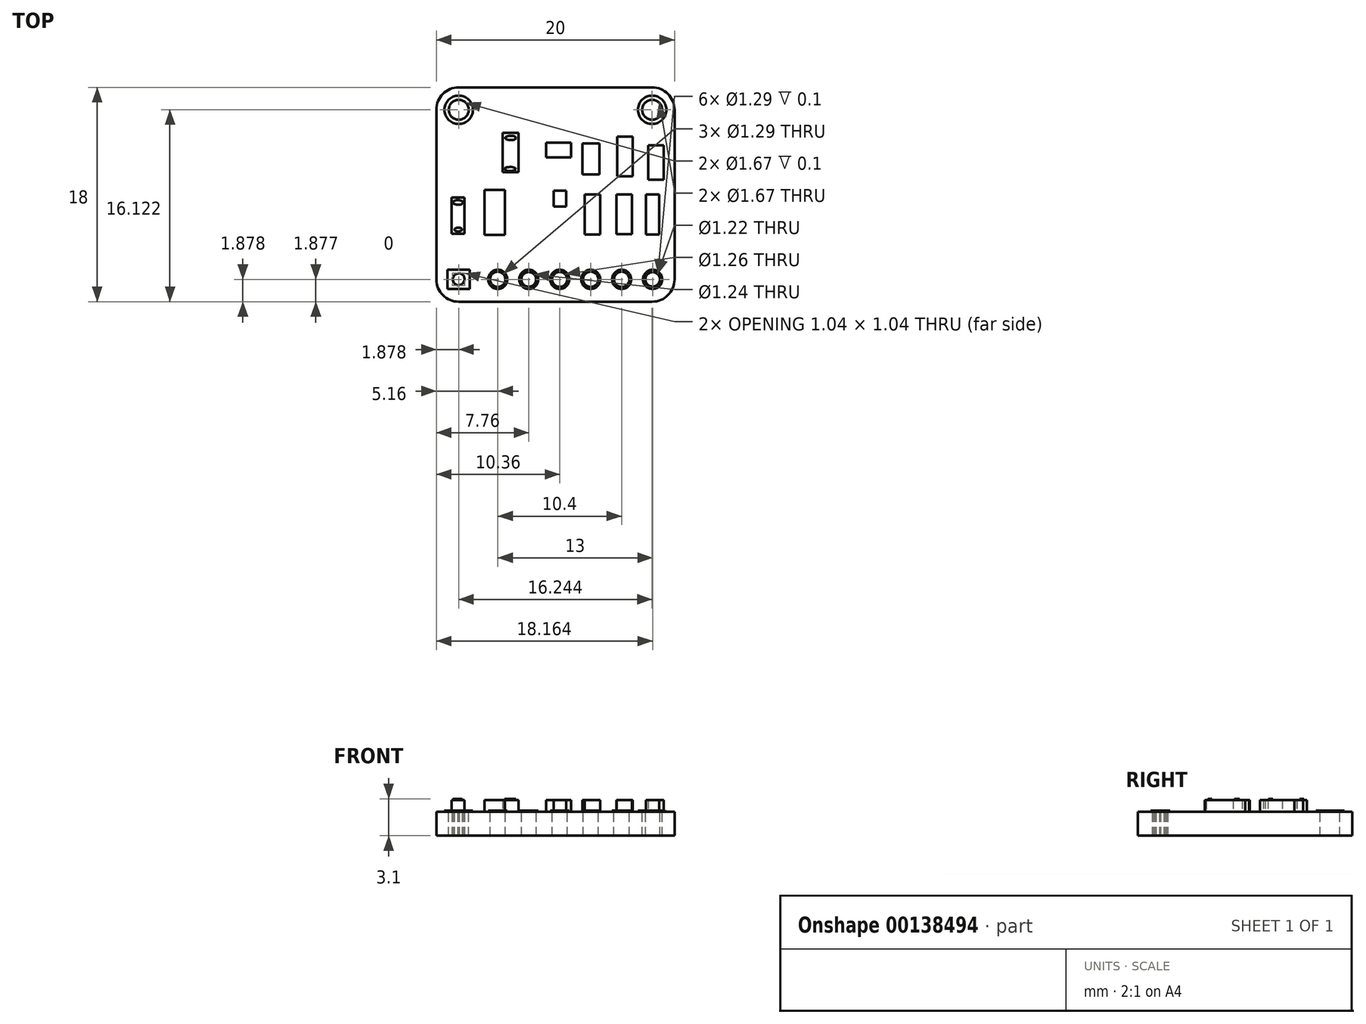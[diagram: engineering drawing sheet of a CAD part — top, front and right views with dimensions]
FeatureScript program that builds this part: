
annotation { "Feature Type Name" : "Feature", "Feature Type Description" : "" }
export const myFeature = defineFeature(function(context is Context, id is Id, definition is map)
    precondition{}
    {
        {
            var Q0;
            Q0=qCreatedBy(makeId("Top.planeOp"),FACE);
            var sketch = newSketch(context, id + "F0", { "sketchPlane" : qUnion([Q0])});
            skLineSegment(sketch, "E0.bottom", {"start": v(10, 9) * mm, "end": v(-10, 9) * mm});
            skLineSegment(sketch, "E0.top", {"start": v(10, -9) * mm, "end": v(-10, -9) * mm});
            skLineSegment(sketch, "E0.left", {"start": v(10, 9) * mm, "end": v(10, -9) * mm});
            skLineSegment(sketch, "E0.right", {"start": v(-10, 9) * mm, "end": v(-10, -9) * mm});
            skPoint(sketch, "E0.middle", {"position": v(0, 0) * mm});
            skSolve(sketch);
        }
        {
            var Q0;
            Q0 = qSketchRegion(id + "F0", true);
            extrude(context, id + "F1", {"entities" : qUnion([Q0]), "oppositeDirection" : true, "depth" : 2 * mm});
        }
        {
            var Q0;
            Q0=makeQuery(id+"F1.opExtrude","SWEPT_EDGE",EDGE,{"disambiguationData":[OSD([sQuery(id+"F0.wireOp",EDGE,"E0.top"),sQuery(id+"F0.wireOp",EDGE,"E0.right")])]});
            var Q1;
            Q1=makeQuery(id+"F1.opExtrude","SWEPT_EDGE",EDGE,{"disambiguationData":[OSD([sQuery(id+"F0.wireOp",EDGE,"E0.top"),sQuery(id+"F0.wireOp",EDGE,"E0.left")])]});
            var Q2;
            Q2=makeQuery(id+"F1.opExtrude","SWEPT_EDGE",EDGE,{"disambiguationData":[OSD([sQuery(id+"F0.wireOp",EDGE,"E0.bottom"),sQuery(id+"F0.wireOp",EDGE,"E0.left")])]});
            var Q3;
            Q3=makeQuery(id+"F1.opExtrude","SWEPT_EDGE",EDGE,{"disambiguationData":[OSD([sQuery(id+"F0.wireOp",EDGE,"E0.bottom"),sQuery(id+"F0.wireOp",EDGE,"E0.right")])]});
            fillet(context, id + "F2", {"entities" : qUnion([Q0, Q1, Q2, Q3]), "radius" : 1.88 * mm, "tangentPropagation" : true, "allowEdgeOverflow" : false});
        }
        {
            var Q0;
            Q0=makeQuery(id+"F1.opExtrude","CAP_FACE",FACE,{"disambiguationData":[OSD([sQuery(id+"F0.wireOp",EDGE,"E0.bottom"),sQuery(id+"F0.wireOp",EDGE,"E0.top"),sQuery(id+"F0.wireOp",EDGE,"E0.left"),sQuery(id+"F0.wireOp",EDGE,"E0.right")])],"isStart":true});
            var sketch = newSketch(context, id + "F3", { "sketchPlane" : qUnion([Q0])});
            skLineSegment(sketch, "E1", {"start": v(-10, 7.12) * mm, "end": v(10, 7.12) * mm, "construction": true});
            skCircle(sketch, "E2", {"center": v(-8.12, 7.12) * mm, "radius": 1.2 * mm});
            skCircle(sketch, "E3", {"center": v(8.12, 7.12) * mm, "radius": 1.2 * mm});
            skCircle(sketch, "E4", {"center": v(-8.12, 7.12) * mm, "radius": 0.84 * mm});
            skCircle(sketch, "E5", {"center": v(8.12, 7.12) * mm, "radius": 0.84 * mm});
            skLineSegment(sketch, "E6", {"start": v(-10, -7.12) * mm, "end": v(10, -7.12) * mm, "construction": true});
            skLineSegment(sketch, "E7.bottom", {"start": v(-7.18, -6.3) * mm, "end": v(-9.06, -6.3) * mm});
            skLineSegment(sketch, "E7.top", {"start": v(-7.18, -7.94) * mm, "end": v(-9.06, -7.94) * mm});
            skLineSegment(sketch, "E7.left", {"start": v(-7.18, -6.3) * mm, "end": v(-7.18, -7.94) * mm});
            skLineSegment(sketch, "E7.right", {"start": v(-9.06, -6.3) * mm, "end": v(-9.06, -7.94) * mm});
            skPoint(sketch, "E7.middle", {"position": v(-8.12, -7.12) * mm});
            skCircle(sketch, "E8.cCircle", {"center": v(-8.12, -7.12) * mm, "radius": 0.48 * mm, "construction": true});
            skLineSegment(sketch, "E8.0", {"start": v(-8.07, -6.6) * mm, "end": v(-7.71, -6.8) * mm});
            skLineSegment(sketch, "E8.1", {"start": v(-7.71, -6.8) * mm, "end": v(-7.6, -7.18) * mm});
            skLineSegment(sketch, "E8.2", {"start": v(-7.6, -7.18) * mm, "end": v(-7.8, -7.53) * mm});
            skLineSegment(sketch, "E8.3", {"start": v(-7.8, -7.53) * mm, "end": v(-8.18, -7.64) * mm});
            skLineSegment(sketch, "E8.4", {"start": v(-8.18, -7.64) * mm, "end": v(-8.53, -7.45) * mm});
            skLineSegment(sketch, "E8.5", {"start": v(-8.53, -7.45) * mm, "end": v(-8.64, -7.07) * mm});
            skLineSegment(sketch, "E8.6", {"start": v(-8.64, -7.07) * mm, "end": v(-8.45, -6.71) * mm});
            skLineSegment(sketch, "E8.7", {"start": v(-8.45, -6.71) * mm, "end": v(-8.07, -6.6) * mm});
            skPoint(sketch, "E8.0.midPoint", {"position": v(-7.9, -6.7) * mm});
            skCircle(sketch, "E9", {"center": v(-4.84, -7.12) * mm, "radius": 0.8 * mm});
            skCircle(sketch, "E10", {"center": v(-2.24, -7.12) * mm, "radius": 0.8 * mm});
            skCircle(sketch, "E11", {"center": v(0.36, -7.12) * mm, "radius": 0.8 * mm});
            skCircle(sketch, "E12", {"center": v(2.96, -7.12) * mm, "radius": 0.8 * mm});
            skCircle(sketch, "E13", {"center": v(5.56, -7.12) * mm, "radius": 0.8 * mm});
            skCircle(sketch, "E14", {"center": v(8.16, -7.12) * mm, "radius": 0.8 * mm});
            skCircle(sketch, "E15", {"center": v(-4.84, -7.12) * mm, "radius": 0.64 * mm});
            skCircle(sketch, "E16", {"center": v(-2.24, -7.12) * mm, "radius": 0.64 * mm});
            skCircle(sketch, "E17", {"center": v(0.36, -7.12) * mm, "radius": 0.64 * mm});
            skCircle(sketch, "E18", {"center": v(2.96, -7.12) * mm, "radius": 0.64 * mm});
            skCircle(sketch, "E19", {"center": v(5.56, -7.12) * mm, "radius": 0.64 * mm});
            skCircle(sketch, "E20", {"center": v(8.16, -7.12) * mm, "radius": 0.64 * mm});
            skCircle(sketch, "E21", {"center": v(-4.84, -7.12) * mm, "radius": 0.6 * mm});
            skCircle(sketch, "E22", {"center": v(-2.24, -7.12) * mm, "radius": 0.62 * mm});
            skCircle(sketch, "E23", {"center": v(0.36, -7.12) * mm, "radius": 0.63 * mm});
            skCircle(sketch, "E24", {"center": v(2.96, -7.12) * mm, "radius": 0.59 * mm});
            skCircle(sketch, "E25", {"center": v(5.56, -7.12) * mm, "radius": 0.6 * mm});
            skCircle(sketch, "E26", {"center": v(8.16, -7.12) * mm, "radius": 0.61 * mm});
            skSolve(sketch);
        }
        {
            var Q0;
            Q0=makeQuery(id+"F3.imprint","IMPRINT",FACE,{"disambiguationData":[TD([[makeQuery(id+"F3.imprint","IMPRINT",EDGE,{"derivedFrom":sQuery(id+"F3.wireOp",EDGE,"E9")}),1.0]])]});
            var Q1;
            Q1=makeQuery(id+"F3.imprint","IMPRINT",FACE,{"disambiguationData":[TD([[makeQuery(id+"F3.imprint","IMPRINT",EDGE,{"derivedFrom":sQuery(id+"F3.wireOp",EDGE,"E10")}),1.0]])]});
            var Q2;
            Q2=makeQuery(id+"F3.imprint","IMPRINT",FACE,{"disambiguationData":[TD([[makeQuery(id+"F3.imprint","IMPRINT",EDGE,{"derivedFrom":sQuery(id+"F3.wireOp",EDGE,"E11")}),1.0]])]});
            var Q3;
            Q3=makeQuery(id+"F3.imprint","IMPRINT",FACE,{"disambiguationData":[TD([[makeQuery(id+"F3.imprint","IMPRINT",EDGE,{"derivedFrom":sQuery(id+"F3.wireOp",EDGE,"E12")}),1.0]])]});
            var Q4;
            Q4=makeQuery(id+"F3.imprint","IMPRINT",FACE,{"disambiguationData":[TD([[makeQuery(id+"F3.imprint","IMPRINT",EDGE,{"derivedFrom":sQuery(id+"F3.wireOp",EDGE,"E13")}),1.0]])]});
            var Q5;
            Q5=makeQuery(id+"F3.imprint","IMPRINT",FACE,{"disambiguationData":[TD([[makeQuery(id+"F3.imprint","IMPRINT",EDGE,{"derivedFrom":sQuery(id+"F3.wireOp",EDGE,"E14")}),1.0]])]});
            var Q6;
            Q6=makeQuery(id+"F3.imprint","IMPRINT",FACE,{"disambiguationData":[TD([[makeQuery(id+"F3.imprint","IMPRINT",EDGE,{"derivedFrom":sQuery(id+"F3.wireOp",EDGE,"E7.bottom")}),1.0]])]});
            var Q7;
            Q7=makeQuery(id+"F3.imprint","IMPRINT",FACE,{"disambiguationData":[TD([[makeQuery(id+"F3.imprint","IMPRINT",EDGE,{"derivedFrom":sQuery(id+"F3.wireOp",EDGE,"E3")}),1.0]])]});
            var Q8;
            Q8=makeQuery(id+"F3.imprint","IMPRINT",FACE,{"disambiguationData":[TD([[makeQuery(id+"F3.imprint","IMPRINT",EDGE,{"derivedFrom":sQuery(id+"F3.wireOp",EDGE,"E2")}),1.0]])]});
            extrude(context, id + "F4", {"entities" : qUnion([Q0, Q1, Q2, Q3, Q4, Q5, Q6, Q7, Q8]), "depth" : .1 * mm});
        }
        {
            var Q0;
            Q0=makeQuery(id+"F3.imprint","IMPRINT",FACE,{"disambiguationData":[TD([[makeQuery(id+"F3.imprint","IMPRINT",EDGE,{"derivedFrom":sQuery(id+"F3.wireOp",EDGE,"E15")}),1.0]])]});
            var Q1;
            Q1=makeQuery(id+"F3.imprint","IMPRINT",FACE,{"disambiguationData":[TD([[makeQuery(id+"F3.imprint","IMPRINT",EDGE,{"derivedFrom":sQuery(id+"F3.wireOp",EDGE,"E8.0")}),-1.0]])]});
            var Q2;
            Q2=makeQuery(id+"F3.imprint","IMPRINT",FACE,{"disambiguationData":[TD([[makeQuery(id+"F3.imprint","IMPRINT",EDGE,{"derivedFrom":sQuery(id+"F3.wireOp",EDGE,"E22")}),1.0]])]});
            var Q3;
            Q3=makeQuery(id+"F3.imprint","IMPRINT",FACE,{"disambiguationData":[TD([[makeQuery(id+"F3.imprint","IMPRINT",EDGE,{"derivedFrom":sQuery(id+"F3.wireOp",EDGE,"E18")}),1.0]])]});
            var Q4;
            Q4=makeQuery(id+"F3.imprint","IMPRINT",FACE,{"disambiguationData":[TD([[makeQuery(id+"F3.imprint","IMPRINT",EDGE,{"derivedFrom":sQuery(id+"F3.wireOp",EDGE,"E23")}),1.0]])]});
            var Q5;
            Q5=makeQuery(id+"F3.imprint","IMPRINT",FACE,{"disambiguationData":[TD([[makeQuery(id+"F3.imprint","IMPRINT",EDGE,{"derivedFrom":sQuery(id+"F3.wireOp",EDGE,"E19")}),1.0]])]});
            var Q6;
            Q6=makeQuery(id+"F3.imprint","IMPRINT",FACE,{"disambiguationData":[TD([[makeQuery(id+"F3.imprint","IMPRINT",EDGE,{"derivedFrom":sQuery(id+"F3.wireOp",EDGE,"E26")}),1.0]])]});
            var Q7;
            Q7=makeQuery(id+"F3.imprint","IMPRINT",FACE,{"disambiguationData":[TD([[makeQuery(id+"F3.imprint","IMPRINT",EDGE,{"derivedFrom":sQuery(id+"F3.wireOp",EDGE,"E21")}),1.0]])]});
            var Q8;
            Q8=makeQuery(id+"F3.imprint","IMPRINT",FACE,{"disambiguationData":[TD([[makeQuery(id+"F3.imprint","IMPRINT",EDGE,{"derivedFrom":sQuery(id+"F3.wireOp",EDGE,"E24")}),1.0]])]});
            var Q9;
            Q9=makeQuery(id+"F3.imprint","IMPRINT",FACE,{"disambiguationData":[TD([[makeQuery(id+"F3.imprint","IMPRINT",EDGE,{"derivedFrom":sQuery(id+"F3.wireOp",EDGE,"E25")}),1.0]])]});
            var Q10;
            Q10=makeQuery(id+"F3.imprint","IMPRINT",FACE,{"disambiguationData":[TD([[makeQuery(id+"F3.imprint","IMPRINT",EDGE,{"derivedFrom":sQuery(id+"F3.wireOp",EDGE,"E5")}),1.0]])]});
            var Q11;
            Q11=makeQuery(id+"F3.imprint","IMPRINT",FACE,{"disambiguationData":[TD([[makeQuery(id+"F3.imprint","IMPRINT",EDGE,{"derivedFrom":sQuery(id+"F3.wireOp",EDGE,"E4")}),1.0]])]});
            extrude(context, id + "F5", {"entities" : qUnion([Q0, Q1, Q2, Q3, Q4, Q5, Q6, Q7, Q8, Q9, Q10, Q11]), "operationType" : NewBodyOperationType.REMOVE, "oppositeDirection" : true, "depth" : 25 * mm});
        }
        {
            var Q0;
            Q0=makeQuery(id+"F3.imprint","IMPRINT",FACE,{"disambiguationData":[TD([[makeQuery(id+"F3.imprint","IMPRINT",EDGE,{"derivedFrom":sQuery(id+"F3.wireOp",EDGE,"E2")}),-1.0]])]});
            var sketch = newSketch(context, id + "F6", { "sketchPlane" : qUnion([Q0])});
            skLineSegment(sketch, "E27", {"start": v(-4.87, -7.14) * mm, "end": v(-4.87, 7.87) * mm, "construction": true});
            skLineSegment(sketch, "E28", {"start": v(-2.22, -7.15) * mm, "end": v(-2.22, 8) * mm, "construction": true});
            skLineSegment(sketch, "E29", {"start": v(0.38, -7.12) * mm, "end": v(0.38, 7.8) * mm, "construction": true});
            skLineSegment(sketch, "E30", {"start": v(2.9, -7.2) * mm, "end": v(2.9, 7.83) * mm, "construction": true});
            skLineSegment(sketch, "E31", {"start": v(5.53, -7.1) * mm, "end": v(5.53, 7.94) * mm, "construction": true});
            skLineSegment(sketch, "E32", {"start": v(8.22, -7.12) * mm, "end": v(8.22, 7.43) * mm, "construction": true});
            skLineSegment(sketch, "E33", {"start": v(-9.22, -2.26) * mm, "end": v(9.5, -2.26) * mm, "construction": true});
            skLineSegment(sketch, "E34", {"start": v(-6.74, 3.73) * mm, "end": v(9.34, 3.73) * mm, "construction": true});
            skLineSegment(sketch, "E35.bottom", {"start": v(-8.71, -3.28) * mm, "end": v(-7.63, -3.28) * mm});
            skLineSegment(sketch, "E35.top", {"start": v(-8.71, -0.25) * mm, "end": v(-7.63, -0.25) * mm});
            skLineSegment(sketch, "E35.left", {"start": v(-8.71, -3.28) * mm, "end": v(-8.71, -0.25) * mm});
            skLineSegment(sketch, "E35.right", {"start": v(-7.63, -3.28) * mm, "end": v(-7.63, -0.25) * mm});
            skLineSegment(sketch, "E36.bottom", {"start": v(-5.97, -3.4) * mm, "end": v(-4.24, -3.4) * mm});
            skLineSegment(sketch, "E36.top", {"start": v(-5.97, 0.38) * mm, "end": v(-4.24, 0.38) * mm});
            skLineSegment(sketch, "E36.left", {"start": v(-5.97, -3.4) * mm, "end": v(-5.97, 0.38) * mm});
            skLineSegment(sketch, "E36.right", {"start": v(-4.24, -3.4) * mm, "end": v(-4.24, 0.38) * mm});
            skLineSegment(sketch, "E37.bottom", {"start": v(-4.42, 1.9) * mm, "end": v(-3.09, 1.9) * mm});
            skLineSegment(sketch, "E37.top", {"start": v(-4.42, 5.18) * mm, "end": v(-3.09, 5.18) * mm});
            skLineSegment(sketch, "E37.left", {"start": v(-4.42, 1.9) * mm, "end": v(-4.42, 5.18) * mm});
            skLineSegment(sketch, "E37.right", {"start": v(-3.09, 1.9) * mm, "end": v(-3.09, 5.18) * mm});
            skLineSegment(sketch, "E38.bottom", {"start": v(0.9, 0.31) * mm, "end": v(-0.14, 0.31) * mm});
            skLineSegment(sketch, "E38.top", {"start": v(0.9, -1.02) * mm, "end": v(-0.14, -1.02) * mm});
            skLineSegment(sketch, "E38.left", {"start": v(0.9, 0.31) * mm, "end": v(0.9, -1.02) * mm});
            skPoint(sketch, "E39.firstSnap0", {"position": v(1.3, 3.73) * mm});
            skLineSegment(sketch, "E39.bottom", {"start": v(1.3, 4.35) * mm, "end": v(-0.78, 4.35) * mm});
            skLineSegment(sketch, "E39.top", {"start": v(1.3, 3.12) * mm, "end": v(-0.78, 3.12) * mm});
            skLineSegment(sketch, "E39.left", {"start": v(1.3, 4.35) * mm, "end": v(1.3, 3.12) * mm});
            skLineSegment(sketch, "E39.right", {"start": v(-0.78, 4.35) * mm, "end": v(-0.78, 3.12) * mm});
            skLineSegment(sketch, "E40.bottom", {"start": v(3.7, 4.31) * mm, "end": v(2.28, 4.31) * mm});
            skLineSegment(sketch, "E40.top", {"start": v(3.7, 1.68) * mm, "end": v(2.28, 1.68) * mm});
            skLineSegment(sketch, "E40.left", {"start": v(3.7, 4.31) * mm, "end": v(3.7, 1.68) * mm});
            skLineSegment(sketch, "E40.right", {"start": v(2.28, 4.31) * mm, "end": v(2.28, 1.68) * mm});
            skLineSegment(sketch, "E41.bottom", {"start": v(2.46, -3.34) * mm, "end": v(3.77, -3.34) * mm});
            skLineSegment(sketch, "E41.top", {"start": v(2.46, 0) * mm, "end": v(3.77, 0) * mm});
            skLineSegment(sketch, "E41.left", {"start": v(2.46, -3.34) * mm, "end": v(2.46, 0) * mm});
            skLineSegment(sketch, "E41.right", {"start": v(3.77, -3.34) * mm, "end": v(3.77, 0) * mm});
            skLineSegment(sketch, "E42.bottom", {"start": v(5.12, 0) * mm, "end": v(6.42, 0) * mm});
            skLineSegment(sketch, "E42.top", {"start": v(5.12, -3.33) * mm, "end": v(6.42, -3.33) * mm});
            skLineSegment(sketch, "E42.left", {"start": v(5.12, 0) * mm, "end": v(5.12, -3.33) * mm});
            skLineSegment(sketch, "E42.right", {"start": v(6.42, 0) * mm, "end": v(6.42, -3.33) * mm});
            skLineSegment(sketch, "E43.bottom", {"start": v(5.2, 4.86) * mm, "end": v(6.5, 4.86) * mm});
            skLineSegment(sketch, "E43.top", {"start": v(5.2, 1.54) * mm, "end": v(6.5, 1.54) * mm});
            skLineSegment(sketch, "E43.left", {"start": v(5.2, 4.86) * mm, "end": v(5.2, 1.54) * mm});
            skLineSegment(sketch, "E43.right", {"start": v(6.5, 4.86) * mm, "end": v(6.5, 1.54) * mm});
            skLineSegment(sketch, "E44.bottom", {"start": v(7.79, 4.13) * mm, "end": v(9.08, 4.13) * mm});
            skLineSegment(sketch, "E44.top", {"start": v(7.79, 1.25) * mm, "end": v(9.08, 1.25) * mm});
            skLineSegment(sketch, "E44.left", {"start": v(7.79, 4.13) * mm, "end": v(7.79, 1.25) * mm});
            skLineSegment(sketch, "E44.right", {"start": v(9.08, 4.13) * mm, "end": v(9.08, 1.25) * mm});
            skLineSegment(sketch, "E45.bottom", {"start": v(7.6, 0) * mm, "end": v(8.72, 0) * mm});
            skLineSegment(sketch, "E45.top", {"start": v(7.6, -3.36) * mm, "end": v(8.72, -3.36) * mm});
            skLineSegment(sketch, "E45.left", {"start": v(7.6, 0) * mm, "end": v(7.6, -3.36) * mm});
            skLineSegment(sketch, "E45.right", {"start": v(8.72, 0) * mm, "end": v(8.72, -3.36) * mm});
            skLineSegment(sketch, "E46.left", {"start": v(-5.97, -3.08) * mm, "end": v(-5.97, -2.59) * mm});
            skLineSegment(sketch, "E47.left", {"start": v(-5.97, -1.6) * mm, "end": v(-5.97, -1.2) * mm});
            skLineSegment(sketch, "E48.left", {"start": v(-5.97, -0.45) * mm, "end": v(-5.97, -0.15) * mm});
            skLineSegment(sketch, "E49.left", {"start": v(-4.24, 0) * mm, "end": v(-4.24, -0.31) * mm});
            skLineSegment(sketch, "E50.left", {"start": v(-4.24, -2.73) * mm, "end": v(-4.24, -3.02) * mm});
            skLineSegment(sketch, "E51.left", {"start": v(0.9, 0.31) * mm, "end": v(0.9, 0.12) * mm});
            skLineSegment(sketch, "E52.left", {"start": v(0.9, -0.13) * mm, "end": v(0.9, -0.31) * mm});
            skLineSegment(sketch, "E53.left", {"start": v(0.9, -0.53) * mm, "end": v(0.9, -0.7) * mm});
            skLineSegment(sketch, "E54.left", {"start": v(0.9, -1.02) * mm, "end": v(0.9, -0.9) * mm});
            skLineSegment(sketch, "E55.MirrorCS", {"start": v(-0.14, 0.31) * mm, "end": v(-0.14, -1.02) * mm});
            skPoint(sketch, "E56.orphan", {"position": v(-0.62, 0.31) * mm});
            skPoint(sketch, "E57.MirrorCS.end.orphan", {"position": v(-0.62, 0.12) * mm});
            skPoint(sketch, "E58.MirrorCS.start.orphan", {"position": v(-0.14, 0.12) * mm});
            skPoint(sketch, "E59.MirrorCS.start.orphan", {"position": v(-0.14, 0.31) * mm});
            skPoint(sketch, "E60.MirrorCS.end.orphan", {"position": v(-0.65, -0.13) * mm});
            skPoint(sketch, "E60.MirrorCS.start.orphan", {"position": v(-0.14, -0.13) * mm});
            skPoint(sketch, "E61.MirrorCS.end.orphan", {"position": v(-0.65, -0.31) * mm});
            skPoint(sketch, "E62.MirrorCS.start.orphan", {"position": v(-0.14, -0.31) * mm});
            skPoint(sketch, "E63.MirrorCS.end.orphan", {"position": v(-0.66, -0.53) * mm});
            skPoint(sketch, "E63.MirrorCS.start.orphan", {"position": v(-0.14, -0.53) * mm});
            skPoint(sketch, "E64.MirrorCS.end.orphan", {"position": v(-0.66, -0.7) * mm});
            skPoint(sketch, "E65.MirrorCS.start.orphan", {"position": v(-0.14, -0.7) * mm});
            skPoint(sketch, "E66.MirrorCS.end.orphan", {"position": v(-0.66, -0.9) * mm});
            skPoint(sketch, "E66.MirrorCS.start.orphan", {"position": v(-0.14, -0.9) * mm});
            skPoint(sketch, "E67.MirrorCS.start.orphan", {"position": v(-0.66, -1.02) * mm});
            skPoint(sketch, "E68.MirrorCS.start.orphan", {"position": v(-0.14, -1.02) * mm});
            skPoint(sketch, "E54.right.end.orphan", {"position": v(1.43, -0.9) * mm});
            skPoint(sketch, "E54.bottom.end.orphan", {"position": v(1.43, -1.02) * mm});
            skPoint(sketch, "E53.right.end.orphan", {"position": v(1.43, -0.7) * mm});
            skPoint(sketch, "E53.right.start.orphan", {"position": v(1.43, -0.53) * mm});
            skPoint(sketch, "E52.bottom.end.orphan", {"position": v(1.42, -0.13) * mm});
            skPoint(sketch, "E52.top.end.orphan", {"position": v(1.42, -0.31) * mm});
            skPoint(sketch, "E51.right.end.orphan", {"position": v(1.39, 0.12) * mm});
            skPoint(sketch, "E51.bottom.end.orphan", {"position": v(1.39, 0.31) * mm});
            skSolve(sketch);
        }
        {
            var Q0;
            Q0 = qSketchRegion(id + "F6", true);
            extrude(context, id + "F7", {"entities" : qUnion([Q0]), "depth" : 1 * mm});
        }
        {
            var Q0;
            Q0=makeQuery(id+"F7.opExtrude","CAP_FACE",FACE,{"disambiguationData":[OSD([sQuery(id+"F6.wireOp",EDGE,"E37.bottom"),sQuery(id+"F6.wireOp",EDGE,"E37.top"),sQuery(id+"F6.wireOp",EDGE,"E37.left"),sQuery(id+"F6.wireOp",EDGE,"E37.right")])],"isStart":false});
            var sketch = newSketch(context, id + "F8", { "sketchPlane" : qUnion([Q0])});
            skEllipse(sketch, "E69", {"center": v(-3.76, 4.76) * mm, "majorRadius": 0.45 * mm, "minorRadius": 0.18 * mm, "majorAxis": v(1, 0)});
            skEllipse(sketch, "E70", {"center": v(-3.8, 2.15) * mm, "majorRadius": 0.46 * mm, "minorRadius": 0.17 * mm, "majorAxis": v(1, 0)});
            skEllipse(sketch, "E71", {"center": v(-8.18, -0.66) * mm, "majorRadius": 0.4 * mm, "minorRadius": 0.2 * mm, "majorAxis": v(1, 0)});
            skEllipse(sketch, "E72", {"center": v(-8.16, -2.94) * mm, "majorRadius": 0.32 * mm, "minorRadius": 0.16 * mm, "majorAxis": v(1, 0)});
            skSolve(sketch);
        }
        {
            var Q0;
            Q0 = qSketchRegion(id + "F8", true);
            extrude(context, id + "F9", {"entities" : qUnion([Q0]), "depth" : .1 * mm});
        }
    });
